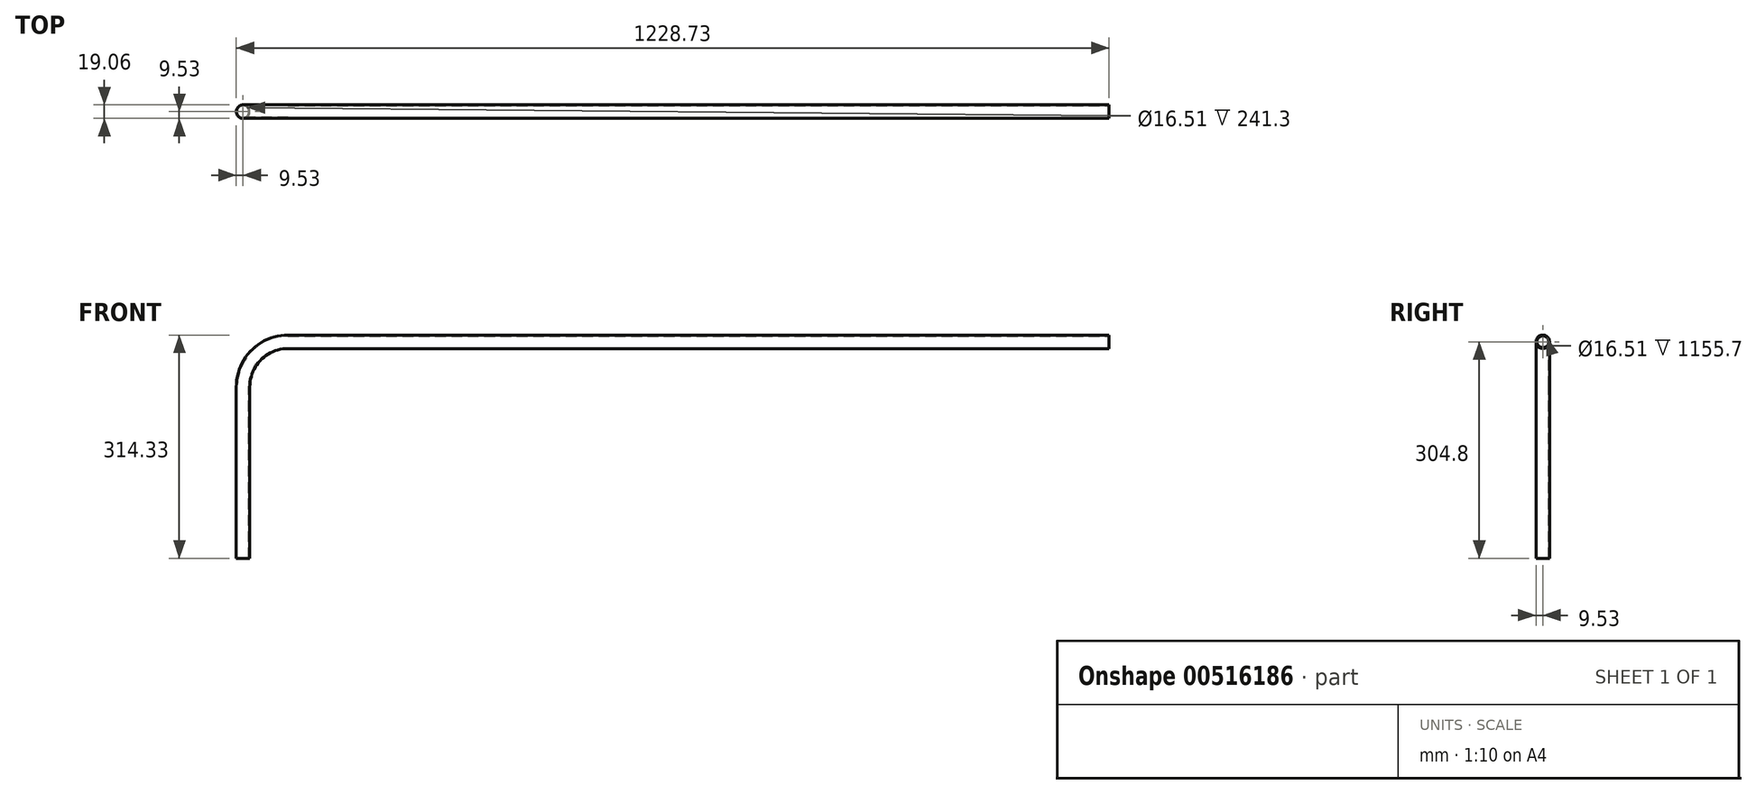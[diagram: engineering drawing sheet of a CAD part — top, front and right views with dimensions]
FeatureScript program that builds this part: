
annotation { "Feature Type Name" : "Feature", "Feature Type Description" : "" }
export const myFeature = defineFeature(function(context is Context, id is Id, definition is map)
    precondition{}
    {
        {
            var Q0;
            Q0=qCreatedBy(makeId("Top.planeOp"),FACE);
            var sketch = newSketch(context, id + "F0", { "sketchPlane" : qUnion([Q0])});
            skCircle(sketch, "E0", {"center": v(0, 0) * mm, "radius": 9.53 * mm});
            skCircle(sketch, "E1", {"center": v(0, 0) * mm, "radius": 8.26 * mm});
            skSolve(sketch);
        }
        {
            var Q0;
            Q0=qCreatedBy(makeId("Front.planeOp"),FACE);
            var sketch = newSketch(context, id + "F1", { "sketchPlane" : qUnion([Q0])});
            skLineSegment(sketch, "E2", {"start": v(0, 0) * mm, "end": v(0, 241.3) * mm});
            skLineSegment(sketch, "E3", {"start": v(63.5, 304.8) * mm, "end": v(1219.2, 304.8) * mm});
            skPoint(sketch, "E4.visualSharp", {"position": v(0, 304.8) * mm});
            skArc(sketch, "E4.filletArc", {"start": v(63.5, 304.8) * mm, "mid": v(18.6, 286.2) * mm, "end": v(0, 241.3) * mm});
            skSolve(sketch);
        }
        {
            var Q0;
            Q0=qSketchRegion(id+"F0",true);
            var Q1;
            Q1=qBodyType(qCreatedBy(id+"F1",EDGE),BodyType.WIRE);
            sweep(context, id + "F2", {"profiles" : qUnion([Q0]), "path" : qUnion([Q1])});
        }
    });
